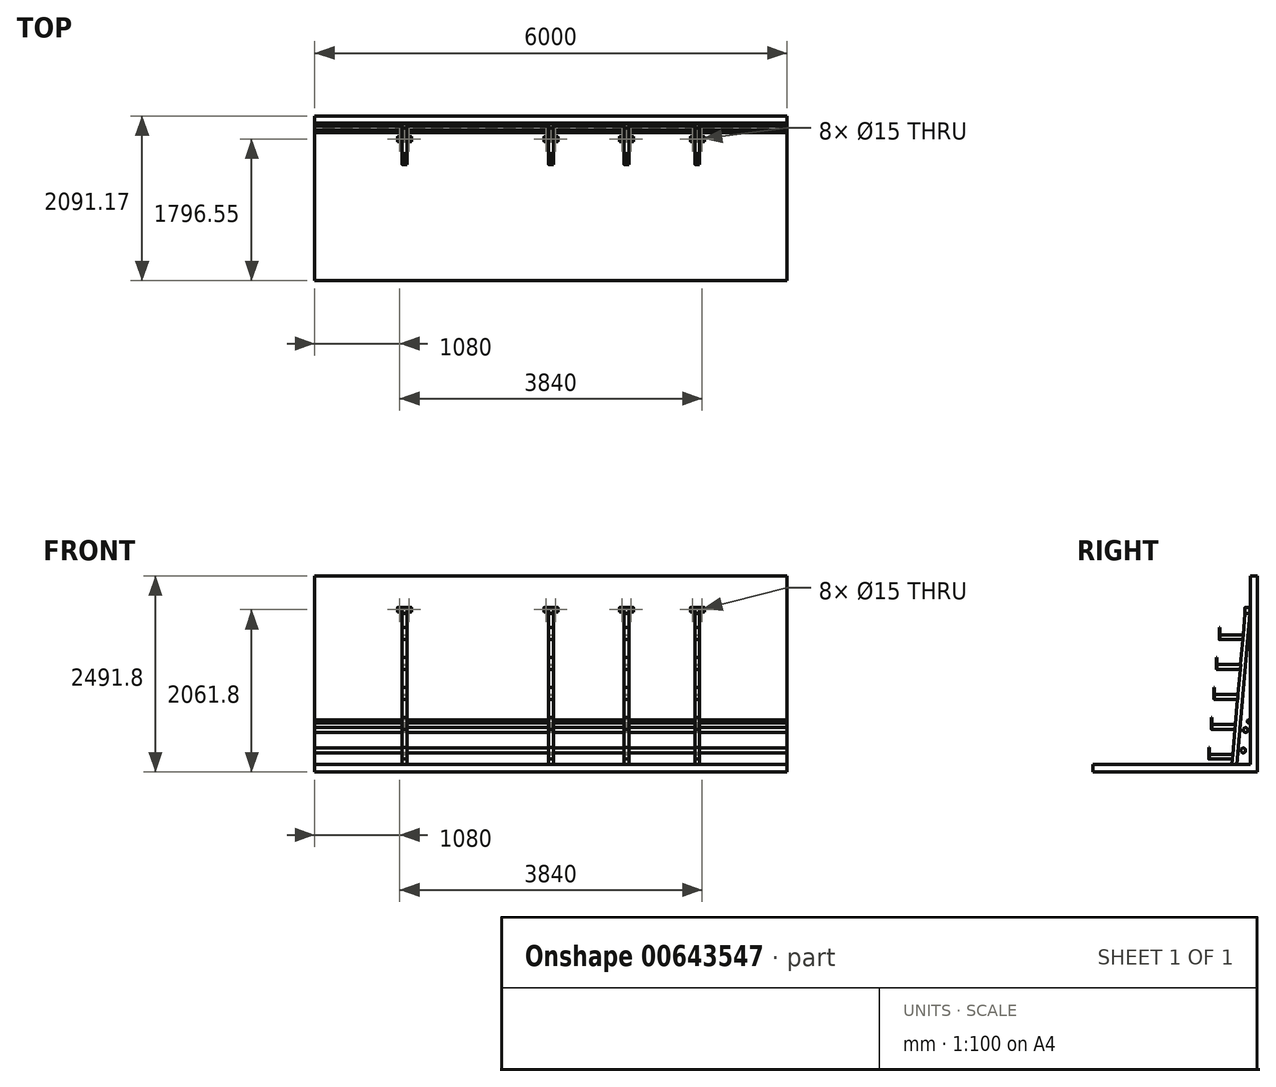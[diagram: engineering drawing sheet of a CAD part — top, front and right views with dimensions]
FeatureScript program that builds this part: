
annotation { "Feature Type Name" : "Feature", "Feature Type Description" : "" }
export const myFeature = defineFeature(function(context is Context, id is Id, definition is map)
    precondition{}
    {
        {
            var Q0;
            Q0=qCreatedBy(makeId("Right.planeOp"),FACE);
            var sketch = newSketch(context, id + "F0", { "sketchPlane" : qUnion([Q0])});
            skLineSegment(sketch, "E0", {"start": v(0, 0) * mm, "end": v(-2000, 0) * mm});
            skLineSegment(sketch, "E1", {"start": v(0, 0) * mm, "end": v(0, 2400) * mm});
            skCircle(sketch, "E2", {"center": v(-60, 440) * mm, "radius": 30 * mm});
            skCircle(sketch, "E3", {"center": v(-20, 550) * mm, "radius": 20 * mm});
            skCircle(sketch, "E4", {"center": v(-90, 180) * mm, "radius": 30 * mm});
            skLineSegment(sketch, "E5.bottom", {"start": v(-2000, 0) * mm, "end": v(0, 0) * mm});
            skLineSegment(sketch, "E5.top", {"start": v(-2000, -91.8) * mm, "end": v(0, -91.8) * mm});
            skLineSegment(sketch, "E5.left", {"start": v(-2000, 0) * mm, "end": v(-2000, -91.8) * mm});
            skLineSegment(sketch, "E6.bottom", {"start": v(0, 2400) * mm, "end": v(91.17, 2400) * mm});
            skLineSegment(sketch, "E6.top", {"start": v(0, -91.8) * mm, "end": v(91.17, -91.8) * mm});
            skLineSegment(sketch, "E6.left", {"start": v(0, 2400) * mm, "end": v(0, 0) * mm});
            skLineSegment(sketch, "E6.right", {"start": v(91.17, 2400) * mm, "end": v(91.17, -91.8) * mm});
            skSolve(sketch);
        }
        {
            var Q0;
            Q0 = qSketchRegion(id + "F0", true);
            extrude(context, id + "F1", {"entities" : qUnion([Q0]), "depth" : 6000 * mm, "offsetDistance" : 25 * mm});
        }
        {
            var Q0;
            Q0=makeQuery(id+"F1.opExtrude","CAP_FACE",FACE,{"disambiguationData":[OSD([sQuery(id+"F0.wireOp",EDGE,"E5.bottom"),sQuery(id+"F0.wireOp",EDGE,"E5.top"),sQuery(id+"F0.wireOp",EDGE,"E5.left"),sQuery(id+"F0.wireOp",EDGE,"E6.bottom"),sQuery(id+"F0.wireOp",EDGE,"E6.top"),sQuery(id+"F0.wireOp",EDGE,"E6.left"),sQuery(id+"F0.wireOp",EDGE,"E6.right")])],"isStart":false});
            var sketch = newSketch(context, id + "F2", { "sketchPlane" : qUnion([Q0])});
            skLineSegment(sketch, "E7", {"start": v(-480, 0) * mm, "end": v(-480, 1226.6) * mm});
            skLineSegment(sketch, "E8", {"start": v(-530, 0) * mm, "end": v(-530, 1239.52) * mm});
            skSolve(sketch);
        }
        {
            var Q0;
            {var subQ1=makeQuery(id+"F1.opExtrude","CAP_EDGE",EDGE,{"disambiguationData":[OSD([sQuery(id+"F0.wireOp",EDGE,"E5.left")])],"isStart":false});Q0=makeQuery(id+"F2.imprint","IMPRINT",FACE,{"disambiguationData":[TD([[makeQuery(id+"F2.imprint","IMPRINT",EDGE,{"derivedFrom":subQ1}),1.0]])]});}
            var sketch = newSketch(context, id + "F3", { "sketchPlane" : qUnion([Q0])});
            skLineSegment(sketch, "E9", {"start": v(-167.45, 6) * mm, "end": v(0, 1920) * mm});
            skLineSegment(sketch, "E10", {"start": v(-227.45, 6) * mm, "end": v(-60, 1920) * mm});
            skLineSegment(sketch, "E11", {"start": v(0, 1920) * mm, "end": v(-60, 1920) * mm});
            skLineSegment(sketch, "E12", {"start": v(-227.45, 6) * mm, "end": v(-167.45, 6) * mm});
            skPoint(sketch, "E13.end.orphan", {"position": v(-167.98, 0) * mm});
            skPoint(sketch, "E13.start.orphan", {"position": v(-227.98, 0) * mm});
            skSolve(sketch);
        }
        {
            var Q0;
            Q0=makeQuery(id+"F3.imprint","IMPRINT",FACE,{"disambiguationData":[TD([[makeQuery(id+"F3.imprint","IMPRINT",EDGE,{"derivedFrom":sQuery(id+"F3.wireOp",EDGE,"E9")}),1.0]])]});
            extrude(context, id + "F4", {"entities" : qUnion([Q0]), "oppositeDirection" : true, "depth" : 60 * mm, "offsetDistance" : 25 * mm});
        }
        {
            var Q0;
            Q0=makeQuery(id+"F4.opExtrude","SWEPT_FACE",FACE,{"disambiguationData":[OSD([sQuery(id+"F3.wireOp",EDGE,"E12")])]});
            var Q1;
            Q1=makeQuery(id+"F4.opExtrude","SWEPT_FACE",FACE,{"disambiguationData":[OSD([sQuery(id+"F3.wireOp",EDGE,"E11")])]});
            shell(context, id + "F5", {"entities" : qUnion([Q0, Q1]), "thickness" : 3 * mm});
        }
        {
            var Q0;
            {var subQ0=sQuery(id+"F3.wireOp",EDGE,"E9");Q0=makeQuery(id+"F5.opShell","OFFSET_EDGE",EDGE,{"disambiguationData":[OSD([subQ0]),TDD([makeQuery(id+"F4.opExtrude","CAP_EDGE",EDGE,{"disambiguationData":[OSD([subQ0])],"isStart":false})])]});}
            var Q1;
            {var subQ0=sQuery(id+"F3.wireOp",EDGE,"E10");Q1=makeQuery(id+"F5.opShell","OFFSET_EDGE",EDGE,{"disambiguationData":[OSD([subQ0]),TDD([makeQuery(id+"F4.opExtrude","CAP_EDGE",EDGE,{"disambiguationData":[OSD([subQ0])],"isStart":false})])]});}
            var Q2;
            {var subQ0=sQuery(id+"F3.wireOp",EDGE,"E9");Q2=makeQuery(id+"F5.opShell","OFFSET_EDGE",EDGE,{"disambiguationData":[OSD([subQ0]),TDD([makeQuery(id+"F4.opExtrude","CAP_EDGE",EDGE,{"disambiguationData":[OSD([subQ0])],"isStart":true})])]});}
            var Q3;
            {var subQ0=sQuery(id+"F3.wireOp",EDGE,"E10");Q3=makeQuery(id+"F5.opShell","OFFSET_EDGE",EDGE,{"disambiguationData":[OSD([subQ0]),TDD([makeQuery(id+"F4.opExtrude","CAP_EDGE",EDGE,{"disambiguationData":[OSD([subQ0])],"isStart":true})])]});}
            fillet(context, id + "F6", {"entities" : qUnion([Q0, Q1, Q2, Q3]), "radius" : 3 * mm, "tangentPropagation" : true, "allowEdgeOverflow" : false});
        }
        {
            var Q0;
            Q0=makeQuery(id+"F4.opExtrude","CAP_EDGE",EDGE,{"disambiguationData":[OSD([sQuery(id+"F3.wireOp",EDGE,"E10")])],"isStart":false});
            var Q1;
            Q1=makeQuery(id+"F4.opExtrude","CAP_EDGE",EDGE,{"disambiguationData":[OSD([sQuery(id+"F3.wireOp",EDGE,"E10")])],"isStart":true});
            var Q2;
            Q2=makeQuery(id+"F4.opExtrude","CAP_EDGE",EDGE,{"disambiguationData":[OSD([sQuery(id+"F3.wireOp",EDGE,"E9")])],"isStart":true});
            var Q3;
            Q3=makeQuery(id+"F4.opExtrude","CAP_EDGE",EDGE,{"disambiguationData":[OSD([sQuery(id+"F3.wireOp",EDGE,"E9")])],"isStart":false});
            fillet(context, id + "F7", {"entities" : qUnion([Q0, Q1, Q2, Q3]), "radius" : 4.5 * mm, "tangentPropagation" : true, "allowEdgeOverflow" : false});
        }
        {
            var Q0;
            Q0=makeQuery(id+"F4.opExtrude","SWEPT_FACE",FACE,{"disambiguationData":[OSD([sQuery(id+"F3.wireOp",EDGE,"E11")])]});
            var sketch = newSketch(context, id + "F8", { "sketchPlane" : qUnion([Q0])});
            skLineSegment(sketch, "E14.0.0", {"start": v(6000, -55.48) * mm, "end": v(6000, -4.52) * mm});
            skEllipticalArc(sketch, "E14.0.1", {});
            skLineSegment(sketch, "E14.0.2", {"start": v(5995.5, 0) * mm, "end": v(5944.5, 0) * mm});
            skEllipticalArc(sketch, "E14.0.3", {});
            skLineSegment(sketch, "E14.0.4", {"start": v(5940, -4.52) * mm, "end": v(5940, -55.48) * mm});
            skEllipticalArc(sketch, "E14.0.5", {});
            skLineSegment(sketch, "E14.0.6", {"start": v(5944.5, -60) * mm, "end": v(5995.5, -60) * mm});
            skEllipticalArc(sketch, "E14.0.7", {});
            skLineSegment(sketch, "E15.0", {"start": v(5946, -56.99) * mm, "end": v(5994, -56.99) * mm});
            skPoint(sketch, "E16.0", {"position": v(5997, -53.98) * mm});
            skEllipticalArc(sketch, "E17.0", {});
            skLineSegment(sketch, "E18.0", {"start": v(5997, -6.02) * mm, "end": v(5997, -53.98) * mm});
            skPoint(sketch, "E19.0", {"position": v(5996.12, -3.9) * mm});
            skEllipticalArc(sketch, "E20.0", {});
            skLineSegment(sketch, "E21.0", {"start": v(5946, -3.01) * mm, "end": v(5994, -3.01) * mm});
            skEllipticalArc(sketch, "E22.0", {});
            skLineSegment(sketch, "E23.0", {"start": v(5943, -6.02) * mm, "end": v(5943, -53.98) * mm});
            skEllipticalArc(sketch, "E24.0", {});
            const initialGuessF8  = {"E14.0.1": [5.9955, -0.0045176047239005035, 0, 1, 0.004517604723900294, 0.0045, 4.71238898038469, 0], "E14.0.3": [5.9445, -0.004517604723900309, 0, -1, 0.004517604723900294, 0.0045, 3.141592653589793, 4.71238898038469], "E14.0.5": [5.9445, -0.05548239527609977, 0, 1, 0.004517604723900294, 0.0045, 1.5707963267948966, 3.141592653589793], "E14.0.7": [5.9955, -0.0554823952760997, 0, -1, 0.004517604723900294, 0.0045, 0, 1.5707963267948966], "E17.0": [5.994, -0.05397652703479969, 0, 1, 0.0030117364826001956, 0.003, 3.141592653589793, 4.71238898038469], "E20.0": [5.994, -0.0060234729652004215, 0, -1, 0.003011736482600195, 0.003, 1.5707963267948966, 3.141592653589793], "E22.0": [5.946, -0.006023472965200574, 0, 1, 0.003011736482600195, 0.003, 0, 1.5707963267948966], "E24.0": [5.946, -0.053976527034799576, 0, -1, 0.0030117364826001956, 0.003, 4.71238898038469, 0]};
            skSetInitialGuess(sketch, initialGuessF8);
            skSolve(sketch);
        }
        {
            var Q0;
            Q0 = qSketchRegion(id + "F8", true);
            extrude(context, id + "F9", {"entities" : qUnion([Q0]), "depth" : 80 * mm, "offsetDistance" : 25 * mm});
        }
        {
            var Q0;
            Q0=makeQuery(id+"F4.opExtrude","CAP_FACE",FACE,{"disambiguationData":[OSD([sQuery(id+"F3.wireOp",EDGE,"E9"),sQuery(id+"F3.wireOp",EDGE,"E10"),sQuery(id+"F3.wireOp",EDGE,"E13"),sQuery(id+"F3.wireOp",EDGE,"E11")])],"isStart":true});
            var sketch = newSketch(context, id + "F10", { "sketchPlane" : qUnion([Q0])});
            skLineSegment(sketch, "E25.0", {"start": v(-228, -0.18) * mm, "end": v(-60, 1920) * mm});
            skLineSegment(sketch, "E26", {"start": v(-221.85, 70) * mm, "end": v(-516.6, 70) * mm});
            skLineSegment(sketch, "E27", {"start": v(-516.6, 70) * mm, "end": v(-516.6, 130) * mm});
            skLineSegment(sketch, "E28", {"start": v(-516.6, 130) * mm, "end": v(-216.6, 130) * mm});
            skLineSegment(sketch, "E29", {"start": v(-216.6, 130) * mm, "end": v(-221.85, 70) * mm});
            skSolve(sketch);
        }
        {
            var Q0;
            Q0 = qSketchRegion(id + "F10", true);
            extrude(context, id + "F11", {"entities" : qUnion([Q0]), "oppositeDirection" : true, "depth" : 60 * mm, "offsetDistance" : 25 * mm});
        }
        {
            var Q0;
            Q0=makeQuery(id+"F11.opExtrude","SWEPT_FACE",FACE,{"disambiguationData":[OSD([sQuery(id+"F10.wireOp",EDGE,"E27")])]});
            var Q1;
            Q1=makeQuery(id+"F11.opExtrude","SWEPT_FACE",FACE,{"disambiguationData":[OSD([sQuery(id+"F10.wireOp",EDGE,"E29")])]});
            shell(context, id + "F12", {"entities" : qUnion([Q0, Q1]), "thickness" : 3 * mm});
        }
        {
            var Q0;
            {var subQ0=sQuery(id+"F10.wireOp",EDGE,"E26");Q0=makeQuery(id+"F12.opShell","OFFSET_EDGE",EDGE,{"disambiguationData":[OSD([subQ0]),TDD([makeQuery(id+"F11.opExtrude","CAP_EDGE",EDGE,{"disambiguationData":[OSD([subQ0])],"isStart":false})])]});}
            var Q1;
            {var subQ0=sQuery(id+"F10.wireOp",EDGE,"E28");Q1=makeQuery(id+"F12.opShell","OFFSET_EDGE",EDGE,{"disambiguationData":[OSD([subQ0]),TDD([makeQuery(id+"F11.opExtrude","CAP_EDGE",EDGE,{"disambiguationData":[OSD([subQ0])],"isStart":false})])]});}
            var Q2;
            {var subQ0=sQuery(id+"F10.wireOp",EDGE,"E28");Q2=makeQuery(id+"F12.opShell","OFFSET_EDGE",EDGE,{"disambiguationData":[OSD([subQ0]),TDD([makeQuery(id+"F11.opExtrude","CAP_EDGE",EDGE,{"disambiguationData":[OSD([subQ0])],"isStart":true})])]});}
            var Q3;
            {var subQ0=sQuery(id+"F10.wireOp",EDGE,"E26");Q3=makeQuery(id+"F12.opShell","OFFSET_EDGE",EDGE,{"disambiguationData":[OSD([subQ0]),TDD([makeQuery(id+"F11.opExtrude","CAP_EDGE",EDGE,{"disambiguationData":[OSD([subQ0])],"isStart":true})])]});}
            fillet(context, id + "F13", {"entities" : qUnion([Q0, Q1, Q2, Q3]), "radius" : 3 * mm, "tangentPropagation" : true, "allowEdgeOverflow" : false});
        }
        {
            var Q0;
            Q0=makeQuery(id+"F11.opExtrude","CAP_EDGE",EDGE,{"disambiguationData":[OSD([sQuery(id+"F10.wireOp",EDGE,"E28")])],"isStart":true});
            var Q1;
            Q1=makeQuery(id+"F11.opExtrude","CAP_EDGE",EDGE,{"disambiguationData":[OSD([sQuery(id+"F10.wireOp",EDGE,"E26")])],"isStart":true});
            var Q2;
            Q2=makeQuery(id+"F11.opExtrude","CAP_EDGE",EDGE,{"disambiguationData":[OSD([sQuery(id+"F10.wireOp",EDGE,"E28")])],"isStart":false});
            var Q3;
            Q3=makeQuery(id+"F11.opExtrude","CAP_EDGE",EDGE,{"disambiguationData":[OSD([sQuery(id+"F10.wireOp",EDGE,"E26")])],"isStart":false});
            fillet(context, id + "F14", {"entities" : qUnion([Q0, Q1, Q2, Q3]), "radius" : 4.5 * mm, "tangentPropagation" : true, "allowEdgeOverflow" : false});
        }
        {
            var Q0;
            Q0=makeQuery(id+"F11.opExtrude","SWEPT_FACE",FACE,{"disambiguationData":[OSD([sQuery(id+"F10.wireOp",EDGE,"E27")])]});
            var sketch = newSketch(context, id + "F15", { "sketchPlane" : qUnion([Q0])});
            skLineSegment(sketch, "E30.bottom", {"start": v(5944.5, 70) * mm, "end": v(5995.5, 70) * mm});
            skLineSegment(sketch, "E30.top", {"start": v(5944.5, 220) * mm, "end": v(5995.5, 220) * mm});
            skLineSegment(sketch, "E30.left", {"start": v(5940, 74.5) * mm, "end": v(5940, 215.5) * mm});
            skLineSegment(sketch, "E30.right", {"start": v(6000, 74.5) * mm, "end": v(6000, 215.5) * mm});
            skPoint(sketch, "E31.visualSharp", {"position": v(5940, 220) * mm});
            skArc(sketch, "E31.filletArc", {"start": v(5944.5, 220) * mm, "mid": v(5941.32, 218.68) * mm, "end": v(5940, 215.5) * mm});
            skPoint(sketch, "E32.visualSharp", {"position": v(6000, 220) * mm});
            skArc(sketch, "E32.filletArc", {"start": v(6000, 215.5) * mm, "mid": v(5998.68, 218.68) * mm, "end": v(5995.5, 220) * mm});
            skPoint(sketch, "E33.visualSharp", {"position": v(6000, 70) * mm});
            skArc(sketch, "E33.filletArc", {"start": v(5995.5, 70) * mm, "mid": v(5998.68, 71.32) * mm, "end": v(6000, 74.5) * mm});
            skPoint(sketch, "E34.visualSharp", {"position": v(5940, 70) * mm});
            skArc(sketch, "E34.filletArc", {"start": v(5940, 74.5) * mm, "mid": v(5941.32, 71.32) * mm, "end": v(5944.5, 70) * mm});
            skSolve(sketch);
        }
        {
            var Q0;
            Q0 = qSketchRegion(id + "F15", true);
            extrude(context, id + "F16", {"entities" : qUnion([Q0]), "depth" : 6 * mm, "offsetDistance" : 25 * mm});
        }
        {
            var Q0;
            Q0=makeQuery(id+"F4.opExtrude","SWEPT_BODY",BODY,{"disambiguationData":[OSD([sQuery(id+"F3.wireOp",EDGE,"E9"),sQuery(id+"F3.wireOp",EDGE,"E10"),sQuery(id+"F3.wireOp",EDGE,"E11"),sQuery(id+"F3.wireOp",EDGE,"E12")])]});
            var Q1;
            Q1=makeQuery(id+"F11.opExtrude","SWEPT_BODY",BODY,{"disambiguationData":[OSD([sQuery(id+"F10.wireOp",EDGE,"E26"),sQuery(id+"F10.wireOp",EDGE,"E27"),sQuery(id+"F10.wireOp",EDGE,"E28"),sQuery(id+"F10.wireOp",EDGE,"E29")])]});
            var Q2;
            Q2=makeQuery(id+"F16.opExtrude","SWEPT_BODY",BODY,{"disambiguationData":[OSD([sQuery(id+"F15.wireOp",EDGE,"E30.bottom"),sQuery(id+"F15.wireOp",EDGE,"E30.top"),sQuery(id+"F15.wireOp",EDGE,"E30.left"),sQuery(id+"F15.wireOp",EDGE,"E30.right"),sQuery(id+"F15.wireOp",EDGE,"E31.filletArc"),sQuery(id+"F15.wireOp",EDGE,"E32.filletArc"),sQuery(id+"F15.wireOp",EDGE,"E33.filletArc"),sQuery(id+"F15.wireOp",EDGE,"E34.filletArc")])]});
            var Q3;
            Q3=makeQuery(id+"F9.opExtrude","SWEPT_BODY",BODY,{"disambiguationData":[OSD([sQuery(id+"F8.wireOp",EDGE,"E14.0.0"),sQuery(id+"F8.wireOp",EDGE,"E14.0.1"),sQuery(id+"F8.wireOp",EDGE,"E14.0.2"),sQuery(id+"F8.wireOp",EDGE,"E14.0.3"),sQuery(id+"F8.wireOp",EDGE,"E14.0.4"),sQuery(id+"F8.wireOp",EDGE,"E14.0.5"),sQuery(id+"F8.wireOp",EDGE,"E14.0.6"),sQuery(id+"F8.wireOp",EDGE,"E14.0.7"),sQuery(id+"F8.wireOp",EDGE,"E15.0"),sQuery(id+"F8.wireOp",EDGE,"E17.0"),sQuery(id+"F8.wireOp",EDGE,"E18.0"),sQuery(id+"F8.wireOp",EDGE,"E20.0"),sQuery(id+"F8.wireOp",EDGE,"E21.0"),sQuery(id+"F8.wireOp",EDGE,"E22.0"),sQuery(id+"F8.wireOp",EDGE,"E23.0"),sQuery(id+"F8.wireOp",EDGE,"E24.0")])]});
            transform(context, id + "F17", {"entities" : qUnion([Q0, Q1, Q2, Q3]), "transformType" : TransformType.TRANSLATION_3D, "dx" : 0 * mm, "dy" : -6 * mm, "dz" : 0 * mm, "makeCopy" : false});
        }
        {
            var Q0;
            Q0=makeQuery(id+"F11.opExtrude","SWEPT_BODY",BODY,{"disambiguationData":[OSD([sQuery(id+"F10.wireOp",EDGE,"E26"),sQuery(id+"F10.wireOp",EDGE,"E27"),sQuery(id+"F10.wireOp",EDGE,"E28"),sQuery(id+"F10.wireOp",EDGE,"E29")])]});
            transform(context, id + "F18", {"entities" : qUnion([Q0]), "transformType" : TransformType.TRANSLATION_3D, "dx" : 0 * mm, "dy" : 33.5 * mm, "dz" : 380 * mm, "makeCopy" : true});
        }
        {
            var Q0;
            Q0=makeQuery(id+"F18.opPattern","COPY",BODY,{"derivedFrom":makeQuery(id+"F11.opExtrude","SWEPT_BODY",BODY,{"disambiguationData":[OSD([sQuery(id+"F10.wireOp",EDGE,"E26"),sQuery(id+"F10.wireOp",EDGE,"E27"),sQuery(id+"F10.wireOp",EDGE,"E28"),sQuery(id+"F10.wireOp",EDGE,"E29")])]}),"instanceName":"1"});
            transform(context, id + "F19", {"entities" : qUnion([Q0]), "transformType" : TransformType.TRANSLATION_3D, "dx" : 0 * mm, "dy" : 33.5 * mm, "dz" : 380 * mm, "makeCopy" : true});
        }
        {
            var Q0;
            Q0=makeQuery(id+"F19.opPattern","COPY",BODY,{"derivedFrom":makeQuery(id+"F18.opPattern","COPY",BODY,{"derivedFrom":makeQuery(id+"F11.opExtrude","SWEPT_BODY",BODY,{"disambiguationData":[OSD([sQuery(id+"F10.wireOp",EDGE,"E26"),sQuery(id+"F10.wireOp",EDGE,"E27"),sQuery(id+"F10.wireOp",EDGE,"E28"),sQuery(id+"F10.wireOp",EDGE,"E29")])]}),"instanceName":"1"}),"instanceName":"1"});
            transform(context, id + "F20", {"entities" : qUnion([Q0]), "transformType" : TransformType.TRANSLATION_3D, "dx" : 0 * mm, "dy" : 33.5 * mm, "dz" : 380 * mm, "makeCopy" : true});
        }
        {
            var Q0;
            Q0=makeQuery(id+"F20.opPattern","COPY",BODY,{"derivedFrom":makeQuery(id+"F19.opPattern","COPY",BODY,{"derivedFrom":makeQuery(id+"F18.opPattern","COPY",BODY,{"derivedFrom":makeQuery(id+"F11.opExtrude","SWEPT_BODY",BODY,{"disambiguationData":[OSD([sQuery(id+"F10.wireOp",EDGE,"E26"),sQuery(id+"F10.wireOp",EDGE,"E27"),sQuery(id+"F10.wireOp",EDGE,"E28"),sQuery(id+"F10.wireOp",EDGE,"E29")])]}),"instanceName":"1"}),"instanceName":"1"}),"instanceName":"1"});
            transform(context, id + "F21", {"entities" : qUnion([Q0]), "transformType" : TransformType.TRANSLATION_3D, "dx" : 0 * mm, "dy" : 33.5 * mm, "dz" : 380 * mm, "makeCopy" : true});
        }
        {
            var Q0;
            Q0=makeQuery(id+"F16.opExtrude","SWEPT_BODY",BODY,{"disambiguationData":[OSD([sQuery(id+"F15.wireOp",EDGE,"E30.bottom"),sQuery(id+"F15.wireOp",EDGE,"E30.top"),sQuery(id+"F15.wireOp",EDGE,"E30.left"),sQuery(id+"F15.wireOp",EDGE,"E30.right"),sQuery(id+"F15.wireOp",EDGE,"E31.filletArc"),sQuery(id+"F15.wireOp",EDGE,"E32.filletArc"),sQuery(id+"F15.wireOp",EDGE,"E33.filletArc"),sQuery(id+"F15.wireOp",EDGE,"E34.filletArc")])]});
            transform(context, id + "F22", {"entities" : qUnion([Q0]), "transformType" : TransformType.TRANSLATION_3D, "dx" : 0 * mm, "dy" : 33.5 * mm, "dz" : 380 * mm, "makeCopy" : true});
        }
        {
            var Q0;
            Q0=makeQuery(id+"F22.opPattern","COPY",BODY,{"derivedFrom":makeQuery(id+"F16.opExtrude","SWEPT_BODY",BODY,{"disambiguationData":[OSD([sQuery(id+"F15.wireOp",EDGE,"E30.bottom"),sQuery(id+"F15.wireOp",EDGE,"E30.top"),sQuery(id+"F15.wireOp",EDGE,"E30.left"),sQuery(id+"F15.wireOp",EDGE,"E30.right"),sQuery(id+"F15.wireOp",EDGE,"E31.filletArc"),sQuery(id+"F15.wireOp",EDGE,"E32.filletArc"),sQuery(id+"F15.wireOp",EDGE,"E33.filletArc"),sQuery(id+"F15.wireOp",EDGE,"E34.filletArc")])]}),"instanceName":"1"});
            transform(context, id + "F23", {"entities" : qUnion([Q0]), "transformType" : TransformType.TRANSLATION_3D, "dx" : 0 * mm, "dy" : 33.5 * mm, "dz" : 380 * mm, "makeCopy" : true});
        }
        {
            var Q0;
            Q0=makeQuery(id+"F23.opPattern","COPY",BODY,{"derivedFrom":makeQuery(id+"F22.opPattern","COPY",BODY,{"derivedFrom":makeQuery(id+"F16.opExtrude","SWEPT_BODY",BODY,{"disambiguationData":[OSD([sQuery(id+"F15.wireOp",EDGE,"E30.bottom"),sQuery(id+"F15.wireOp",EDGE,"E30.top"),sQuery(id+"F15.wireOp",EDGE,"E30.left"),sQuery(id+"F15.wireOp",EDGE,"E30.right"),sQuery(id+"F15.wireOp",EDGE,"E31.filletArc"),sQuery(id+"F15.wireOp",EDGE,"E32.filletArc"),sQuery(id+"F15.wireOp",EDGE,"E33.filletArc"),sQuery(id+"F15.wireOp",EDGE,"E34.filletArc")])]}),"instanceName":"1"}),"instanceName":"1"});
            transform(context, id + "F24", {"entities" : qUnion([Q0]), "transformType" : TransformType.TRANSLATION_3D, "dx" : 0 * mm, "dy" : 33.5 * mm, "dz" : 380 * mm, "makeCopy" : true});
        }
        {
            var Q0;
            Q0=makeQuery(id+"F24.opPattern","COPY",BODY,{"derivedFrom":makeQuery(id+"F23.opPattern","COPY",BODY,{"derivedFrom":makeQuery(id+"F22.opPattern","COPY",BODY,{"derivedFrom":makeQuery(id+"F16.opExtrude","SWEPT_BODY",BODY,{"disambiguationData":[OSD([sQuery(id+"F15.wireOp",EDGE,"E30.bottom"),sQuery(id+"F15.wireOp",EDGE,"E30.top"),sQuery(id+"F15.wireOp",EDGE,"E30.left"),sQuery(id+"F15.wireOp",EDGE,"E30.right"),sQuery(id+"F15.wireOp",EDGE,"E31.filletArc"),sQuery(id+"F15.wireOp",EDGE,"E32.filletArc"),sQuery(id+"F15.wireOp",EDGE,"E33.filletArc"),sQuery(id+"F15.wireOp",EDGE,"E34.filletArc")])]}),"instanceName":"1"}),"instanceName":"1"}),"instanceName":"1"});
            transform(context, id + "F25", {"entities" : qUnion([Q0]), "transformType" : TransformType.TRANSLATION_3D, "dx" : 0 * mm, "dy" : 33.5 * mm, "dz" : 380 * mm, "makeCopy" : true});
        }
        {
            var Q0;
            Q0=makeQuery(id+"F4.opExtrude","SWEPT_FACE",FACE,{"disambiguationData":[OSD([sQuery(id+"F3.wireOp",EDGE,"E12")])]});
            var sketch = newSketch(context, id + "F26", { "sketchPlane" : qUnion([Q0])});
            skLineSegment(sketch, "E35.bottom", {"start": v(6055.5, 173.45) * mm, "end": v(5884.5, 173.45) * mm});
            skLineSegment(sketch, "E35.top", {"start": v(6055.5, 233.45) * mm, "end": v(5884.5, 233.45) * mm});
            skLineSegment(sketch, "E35.left", {"start": v(6060, 177.95) * mm, "end": v(6060, 228.95) * mm});
            skLineSegment(sketch, "E35.right", {"start": v(5880, 177.95) * mm, "end": v(5880, 228.95) * mm});
            skPoint(sketch, "E36.visualSharp", {"position": v(6060, 173.45) * mm});
            skArc(sketch, "E36.filletArc", {"start": v(6055.5, 173.45) * mm, "mid": v(6058.68, 174.77) * mm, "end": v(6060, 177.95) * mm});
            skPoint(sketch, "E37.visualSharp", {"position": v(6060, 233.45) * mm});
            skArc(sketch, "E37.filletArc", {"start": v(6060, 228.95) * mm, "mid": v(6058.68, 232.14) * mm, "end": v(6055.5, 233.45) * mm});
            skPoint(sketch, "E38.visualSharp", {"position": v(5880, 233.45) * mm});
            skArc(sketch, "E38.filletArc", {"start": v(5884.5, 233.45) * mm, "mid": v(5881.32, 232.14) * mm, "end": v(5880, 228.95) * mm});
            skPoint(sketch, "E39.visualSharp", {"position": v(5880, 173.45) * mm});
            skArc(sketch, "E39.filletArc", {"start": v(5880, 177.95) * mm, "mid": v(5881.32, 174.77) * mm, "end": v(5884.5, 173.45) * mm});
            skCircle(sketch, "E40", {"center": v(6030, 203.45) * mm, "radius": 7.5 * mm});
            skCircle(sketch, "E41", {"center": v(5910, 203.45) * mm, "radius": 7.5 * mm});
            skSolve(sketch);
        }
        {
            var Q0;
            Q0 = qSketchRegion(id + "F26", true);
            extrude(context, id + "F27", {"entities" : qUnion([Q0]), "depth" : 6 * mm, "offsetDistance" : 25 * mm});
        }
        {
            var Q0;
            Q0=makeQuery(id+"F9.opExtrude","SWEPT_FACE",FACE,{"disambiguationData":[OSD([sQuery(id+"F8.wireOp",EDGE,"E14.0.2")])]});
            var sketch = newSketch(context, id + "F28", { "sketchPlane" : qUnion([Q0])});
            skLineSegment(sketch, "E42.bottom", {"start": v(-5884.5, 1940) * mm, "end": v(-6055.5, 1940) * mm});
            skLineSegment(sketch, "E42.top", {"start": v(-5884.5, 2000) * mm, "end": v(-6055.5, 2000) * mm});
            skLineSegment(sketch, "E42.left", {"start": v(-5880, 1944.5) * mm, "end": v(-5880, 1995.5) * mm});
            skLineSegment(sketch, "E42.right", {"start": v(-6060, 1944.5) * mm, "end": v(-6060, 1995.5) * mm});
            skCircle(sketch, "E43", {"center": v(-5910, 1970) * mm, "radius": 7.5 * mm});
            skCircle(sketch, "E44", {"center": v(-6030, 1970) * mm, "radius": 7.5 * mm});
            skPoint(sketch, "E45.visualSharp", {"position": v(-5880, 1940) * mm});
            skArc(sketch, "E45.filletArc", {"start": v(-5884.5, 1940) * mm, "mid": v(-5881.32, 1941.32) * mm, "end": v(-5880, 1944.5) * mm});
            skPoint(sketch, "E46.visualSharp", {"position": v(-5880, 2000) * mm});
            skArc(sketch, "E46.filletArc", {"start": v(-5880, 1995.5) * mm, "mid": v(-5881.32, 1998.68) * mm, "end": v(-5884.5, 2000) * mm});
            skPoint(sketch, "E47.visualSharp", {"position": v(-6060, 2000) * mm});
            skArc(sketch, "E47.filletArc", {"start": v(-6055.5, 2000) * mm, "mid": v(-6058.68, 1998.68) * mm, "end": v(-6060, 1995.5) * mm});
            skPoint(sketch, "E48.visualSharp", {"position": v(-6060, 1940) * mm});
            skArc(sketch, "E48.filletArc", {"start": v(-6060, 1944.5) * mm, "mid": v(-6058.68, 1941.32) * mm, "end": v(-6055.5, 1940) * mm});
            skSolve(sketch);
        }
        {
            var Q0;
            Q0 = qSketchRegion(id + "F28", true);
            extrude(context, id + "F29", {"entities" : qUnion([Q0]), "depth" : 6 * mm, "offsetDistance" : 25 * mm});
        }
        {
            var Q0;
            Q0=makeQuery(id+"F4.opExtrude","SWEPT_BODY",BODY,{"disambiguationData":[OSD([sQuery(id+"F3.wireOp",EDGE,"E9"),sQuery(id+"F3.wireOp",EDGE,"E10"),sQuery(id+"F3.wireOp",EDGE,"E11"),sQuery(id+"F3.wireOp",EDGE,"E12")])]});
            var Q1;
            Q1=makeQuery(id+"F9.opExtrude","SWEPT_BODY",BODY,{"disambiguationData":[OSD([sQuery(id+"F8.wireOp",EDGE,"E14.0.0"),sQuery(id+"F8.wireOp",EDGE,"E14.0.1"),sQuery(id+"F8.wireOp",EDGE,"E14.0.2"),sQuery(id+"F8.wireOp",EDGE,"E14.0.3"),sQuery(id+"F8.wireOp",EDGE,"E14.0.4"),sQuery(id+"F8.wireOp",EDGE,"E14.0.5"),sQuery(id+"F8.wireOp",EDGE,"E14.0.6"),sQuery(id+"F8.wireOp",EDGE,"E14.0.7"),sQuery(id+"F8.wireOp",EDGE,"E15.0"),sQuery(id+"F8.wireOp",EDGE,"E17.0"),sQuery(id+"F8.wireOp",EDGE,"E18.0"),sQuery(id+"F8.wireOp",EDGE,"E20.0"),sQuery(id+"F8.wireOp",EDGE,"E21.0"),sQuery(id+"F8.wireOp",EDGE,"E22.0"),sQuery(id+"F8.wireOp",EDGE,"E23.0"),sQuery(id+"F8.wireOp",EDGE,"E24.0")])]});
            var Q2;
            Q2=makeQuery(id+"F21.opPattern","COPY",BODY,{"derivedFrom":makeQuery(id+"F20.opPattern","COPY",BODY,{"derivedFrom":makeQuery(id+"F19.opPattern","COPY",BODY,{"derivedFrom":makeQuery(id+"F18.opPattern","COPY",BODY,{"derivedFrom":makeQuery(id+"F11.opExtrude","SWEPT_BODY",BODY,{"disambiguationData":[OSD([sQuery(id+"F10.wireOp",EDGE,"E26"),sQuery(id+"F10.wireOp",EDGE,"E27"),sQuery(id+"F10.wireOp",EDGE,"E28"),sQuery(id+"F10.wireOp",EDGE,"E29")])]}),"instanceName":"1"}),"instanceName":"1"}),"instanceName":"1"}),"instanceName":"1"});
            var Q3;
            Q3=makeQuery(id+"F25.opPattern","COPY",BODY,{"derivedFrom":makeQuery(id+"F24.opPattern","COPY",BODY,{"derivedFrom":makeQuery(id+"F23.opPattern","COPY",BODY,{"derivedFrom":makeQuery(id+"F22.opPattern","COPY",BODY,{"derivedFrom":makeQuery(id+"F16.opExtrude","SWEPT_BODY",BODY,{"disambiguationData":[OSD([sQuery(id+"F15.wireOp",EDGE,"E30.bottom"),sQuery(id+"F15.wireOp",EDGE,"E30.top"),sQuery(id+"F15.wireOp",EDGE,"E30.left"),sQuery(id+"F15.wireOp",EDGE,"E30.right"),sQuery(id+"F15.wireOp",EDGE,"E31.filletArc"),sQuery(id+"F15.wireOp",EDGE,"E32.filletArc"),sQuery(id+"F15.wireOp",EDGE,"E33.filletArc"),sQuery(id+"F15.wireOp",EDGE,"E34.filletArc")])]}),"instanceName":"1"}),"instanceName":"1"}),"instanceName":"1"}),"instanceName":"1"});
            var Q4;
            Q4=makeQuery(id+"F24.opPattern","COPY",BODY,{"derivedFrom":makeQuery(id+"F23.opPattern","COPY",BODY,{"derivedFrom":makeQuery(id+"F22.opPattern","COPY",BODY,{"derivedFrom":makeQuery(id+"F16.opExtrude","SWEPT_BODY",BODY,{"disambiguationData":[OSD([sQuery(id+"F15.wireOp",EDGE,"E30.bottom"),sQuery(id+"F15.wireOp",EDGE,"E30.top"),sQuery(id+"F15.wireOp",EDGE,"E30.left"),sQuery(id+"F15.wireOp",EDGE,"E30.right"),sQuery(id+"F15.wireOp",EDGE,"E31.filletArc"),sQuery(id+"F15.wireOp",EDGE,"E32.filletArc"),sQuery(id+"F15.wireOp",EDGE,"E33.filletArc"),sQuery(id+"F15.wireOp",EDGE,"E34.filletArc")])]}),"instanceName":"1"}),"instanceName":"1"}),"instanceName":"1"});
            var Q5;
            Q5=makeQuery(id+"F20.opPattern","COPY",BODY,{"derivedFrom":makeQuery(id+"F19.opPattern","COPY",BODY,{"derivedFrom":makeQuery(id+"F18.opPattern","COPY",BODY,{"derivedFrom":makeQuery(id+"F11.opExtrude","SWEPT_BODY",BODY,{"disambiguationData":[OSD([sQuery(id+"F10.wireOp",EDGE,"E26"),sQuery(id+"F10.wireOp",EDGE,"E27"),sQuery(id+"F10.wireOp",EDGE,"E28"),sQuery(id+"F10.wireOp",EDGE,"E29")])]}),"instanceName":"1"}),"instanceName":"1"}),"instanceName":"1"});
            var Q6;
            Q6=makeQuery(id+"F19.opPattern","COPY",BODY,{"derivedFrom":makeQuery(id+"F18.opPattern","COPY",BODY,{"derivedFrom":makeQuery(id+"F11.opExtrude","SWEPT_BODY",BODY,{"disambiguationData":[OSD([sQuery(id+"F10.wireOp",EDGE,"E26"),sQuery(id+"F10.wireOp",EDGE,"E27"),sQuery(id+"F10.wireOp",EDGE,"E28"),sQuery(id+"F10.wireOp",EDGE,"E29")])]}),"instanceName":"1"}),"instanceName":"1"});
            var Q7;
            Q7=makeQuery(id+"F23.opPattern","COPY",BODY,{"derivedFrom":makeQuery(id+"F22.opPattern","COPY",BODY,{"derivedFrom":makeQuery(id+"F16.opExtrude","SWEPT_BODY",BODY,{"disambiguationData":[OSD([sQuery(id+"F15.wireOp",EDGE,"E30.bottom"),sQuery(id+"F15.wireOp",EDGE,"E30.top"),sQuery(id+"F15.wireOp",EDGE,"E30.left"),sQuery(id+"F15.wireOp",EDGE,"E30.right"),sQuery(id+"F15.wireOp",EDGE,"E31.filletArc"),sQuery(id+"F15.wireOp",EDGE,"E32.filletArc"),sQuery(id+"F15.wireOp",EDGE,"E33.filletArc"),sQuery(id+"F15.wireOp",EDGE,"E34.filletArc")])]}),"instanceName":"1"}),"instanceName":"1"});
            var Q8;
            Q8=makeQuery(id+"F22.opPattern","COPY",BODY,{"derivedFrom":makeQuery(id+"F16.opExtrude","SWEPT_BODY",BODY,{"disambiguationData":[OSD([sQuery(id+"F15.wireOp",EDGE,"E30.bottom"),sQuery(id+"F15.wireOp",EDGE,"E30.top"),sQuery(id+"F15.wireOp",EDGE,"E30.left"),sQuery(id+"F15.wireOp",EDGE,"E30.right"),sQuery(id+"F15.wireOp",EDGE,"E31.filletArc"),sQuery(id+"F15.wireOp",EDGE,"E32.filletArc"),sQuery(id+"F15.wireOp",EDGE,"E33.filletArc"),sQuery(id+"F15.wireOp",EDGE,"E34.filletArc")])]}),"instanceName":"1"});
            var Q9;
            Q9=makeQuery(id+"F18.opPattern","COPY",BODY,{"derivedFrom":makeQuery(id+"F11.opExtrude","SWEPT_BODY",BODY,{"disambiguationData":[OSD([sQuery(id+"F10.wireOp",EDGE,"E26"),sQuery(id+"F10.wireOp",EDGE,"E27"),sQuery(id+"F10.wireOp",EDGE,"E28"),sQuery(id+"F10.wireOp",EDGE,"E29")])]}),"instanceName":"1"});
            var Q10;
            Q10=makeQuery(id+"F11.opExtrude","SWEPT_BODY",BODY,{"disambiguationData":[OSD([sQuery(id+"F10.wireOp",EDGE,"E26"),sQuery(id+"F10.wireOp",EDGE,"E27"),sQuery(id+"F10.wireOp",EDGE,"E28"),sQuery(id+"F10.wireOp",EDGE,"E29")])]});
            var Q11;
            Q11=makeQuery(id+"F16.opExtrude","SWEPT_BODY",BODY,{"disambiguationData":[OSD([sQuery(id+"F15.wireOp",EDGE,"E30.bottom"),sQuery(id+"F15.wireOp",EDGE,"E30.top"),sQuery(id+"F15.wireOp",EDGE,"E30.left"),sQuery(id+"F15.wireOp",EDGE,"E30.right"),sQuery(id+"F15.wireOp",EDGE,"E31.filletArc"),sQuery(id+"F15.wireOp",EDGE,"E32.filletArc"),sQuery(id+"F15.wireOp",EDGE,"E33.filletArc"),sQuery(id+"F15.wireOp",EDGE,"E34.filletArc")])]});
            var Q12;
            Q12=makeQuery(id+"F27.opExtrude","SWEPT_BODY",BODY,{"disambiguationData":[OSD([sQuery(id+"F26.wireOp",EDGE,"E35.bottom"),sQuery(id+"F26.wireOp",EDGE,"E35.top"),sQuery(id+"F26.wireOp",EDGE,"E35.left"),sQuery(id+"F26.wireOp",EDGE,"E35.right"),sQuery(id+"F26.wireOp",EDGE,"E36.filletArc"),sQuery(id+"F26.wireOp",EDGE,"E37.filletArc"),sQuery(id+"F26.wireOp",EDGE,"E38.filletArc"),sQuery(id+"F26.wireOp",EDGE,"E39.filletArc"),sQuery(id+"F26.wireOp",EDGE,"E40"),sQuery(id+"F26.wireOp",EDGE,"E41")])]});
            var Q13;
            Q13=makeQuery(id+"F29.opExtrude","SWEPT_BODY",BODY,{"disambiguationData":[OSD([sQuery(id+"F28.wireOp",EDGE,"E42.bottom"),sQuery(id+"F28.wireOp",EDGE,"E42.top"),sQuery(id+"F28.wireOp",EDGE,"E42.left"),sQuery(id+"F28.wireOp",EDGE,"E42.right"),sQuery(id+"F28.wireOp",EDGE,"E43"),sQuery(id+"F28.wireOp",EDGE,"E44"),sQuery(id+"F28.wireOp",EDGE,"E45.filletArc"),sQuery(id+"F28.wireOp",EDGE,"E46.filletArc"),sQuery(id+"F28.wireOp",EDGE,"E47.filletArc"),sQuery(id+"F28.wireOp",EDGE,"E48.filletArc")])]});
            transform(context, id + "F30", {"entities" : qUnion([Q0, Q1, Q2, Q3, Q4, Q5, Q6, Q7, Q8, Q9, Q10, Q11, Q12, Q13]), "transformType" : TransformType.TRANSLATION_3D, "dx" : -2970 * mm, "dy" : 0 * mm, "dz" : 0 * mm, "makeCopy" : false});
        }
        {
            var Q0;
            Q0=makeQuery(id+"F9.opExtrude","SWEPT_BODY",BODY,{"disambiguationData":[OSD([sQuery(id+"F8.wireOp",EDGE,"E14.0.0"),sQuery(id+"F8.wireOp",EDGE,"E14.0.1"),sQuery(id+"F8.wireOp",EDGE,"E14.0.2"),sQuery(id+"F8.wireOp",EDGE,"E14.0.3"),sQuery(id+"F8.wireOp",EDGE,"E14.0.4"),sQuery(id+"F8.wireOp",EDGE,"E14.0.5"),sQuery(id+"F8.wireOp",EDGE,"E14.0.6"),sQuery(id+"F8.wireOp",EDGE,"E14.0.7"),sQuery(id+"F8.wireOp",EDGE,"E15.0"),sQuery(id+"F8.wireOp",EDGE,"E17.0"),sQuery(id+"F8.wireOp",EDGE,"E18.0"),sQuery(id+"F8.wireOp",EDGE,"E20.0"),sQuery(id+"F8.wireOp",EDGE,"E21.0"),sQuery(id+"F8.wireOp",EDGE,"E22.0"),sQuery(id+"F8.wireOp",EDGE,"E23.0"),sQuery(id+"F8.wireOp",EDGE,"E24.0")])]});
            var Q1;
            Q1=makeQuery(id+"F4.opExtrude","SWEPT_BODY",BODY,{"disambiguationData":[OSD([sQuery(id+"F3.wireOp",EDGE,"E9"),sQuery(id+"F3.wireOp",EDGE,"E10"),sQuery(id+"F3.wireOp",EDGE,"E11"),sQuery(id+"F3.wireOp",EDGE,"E12")])]});
            var Q2;
            Q2=makeQuery(id+"F21.opPattern","COPY",BODY,{"derivedFrom":makeQuery(id+"F20.opPattern","COPY",BODY,{"derivedFrom":makeQuery(id+"F19.opPattern","COPY",BODY,{"derivedFrom":makeQuery(id+"F18.opPattern","COPY",BODY,{"derivedFrom":makeQuery(id+"F11.opExtrude","SWEPT_BODY",BODY,{"disambiguationData":[OSD([sQuery(id+"F10.wireOp",EDGE,"E26"),sQuery(id+"F10.wireOp",EDGE,"E27"),sQuery(id+"F10.wireOp",EDGE,"E28"),sQuery(id+"F10.wireOp",EDGE,"E29")])]}),"instanceName":"1"}),"instanceName":"1"}),"instanceName":"1"}),"instanceName":"1"});
            var Q3;
            Q3=makeQuery(id+"F25.opPattern","COPY",BODY,{"derivedFrom":makeQuery(id+"F24.opPattern","COPY",BODY,{"derivedFrom":makeQuery(id+"F23.opPattern","COPY",BODY,{"derivedFrom":makeQuery(id+"F22.opPattern","COPY",BODY,{"derivedFrom":makeQuery(id+"F16.opExtrude","SWEPT_BODY",BODY,{"disambiguationData":[OSD([sQuery(id+"F15.wireOp",EDGE,"E30.bottom"),sQuery(id+"F15.wireOp",EDGE,"E30.top"),sQuery(id+"F15.wireOp",EDGE,"E30.left"),sQuery(id+"F15.wireOp",EDGE,"E30.right"),sQuery(id+"F15.wireOp",EDGE,"E31.filletArc"),sQuery(id+"F15.wireOp",EDGE,"E32.filletArc"),sQuery(id+"F15.wireOp",EDGE,"E33.filletArc"),sQuery(id+"F15.wireOp",EDGE,"E34.filletArc")])]}),"instanceName":"1"}),"instanceName":"1"}),"instanceName":"1"}),"instanceName":"1"});
            var Q4;
            Q4=makeQuery(id+"F24.opPattern","COPY",BODY,{"derivedFrom":makeQuery(id+"F23.opPattern","COPY",BODY,{"derivedFrom":makeQuery(id+"F22.opPattern","COPY",BODY,{"derivedFrom":makeQuery(id+"F16.opExtrude","SWEPT_BODY",BODY,{"disambiguationData":[OSD([sQuery(id+"F15.wireOp",EDGE,"E30.bottom"),sQuery(id+"F15.wireOp",EDGE,"E30.top"),sQuery(id+"F15.wireOp",EDGE,"E30.left"),sQuery(id+"F15.wireOp",EDGE,"E30.right"),sQuery(id+"F15.wireOp",EDGE,"E31.filletArc"),sQuery(id+"F15.wireOp",EDGE,"E32.filletArc"),sQuery(id+"F15.wireOp",EDGE,"E33.filletArc"),sQuery(id+"F15.wireOp",EDGE,"E34.filletArc")])]}),"instanceName":"1"}),"instanceName":"1"}),"instanceName":"1"});
            var Q5;
            Q5=makeQuery(id+"F20.opPattern","COPY",BODY,{"derivedFrom":makeQuery(id+"F19.opPattern","COPY",BODY,{"derivedFrom":makeQuery(id+"F18.opPattern","COPY",BODY,{"derivedFrom":makeQuery(id+"F11.opExtrude","SWEPT_BODY",BODY,{"disambiguationData":[OSD([sQuery(id+"F10.wireOp",EDGE,"E26"),sQuery(id+"F10.wireOp",EDGE,"E27"),sQuery(id+"F10.wireOp",EDGE,"E28"),sQuery(id+"F10.wireOp",EDGE,"E29")])]}),"instanceName":"1"}),"instanceName":"1"}),"instanceName":"1"});
            var Q6;
            Q6=makeQuery(id+"F23.opPattern","COPY",BODY,{"derivedFrom":makeQuery(id+"F22.opPattern","COPY",BODY,{"derivedFrom":makeQuery(id+"F16.opExtrude","SWEPT_BODY",BODY,{"disambiguationData":[OSD([sQuery(id+"F15.wireOp",EDGE,"E30.bottom"),sQuery(id+"F15.wireOp",EDGE,"E30.top"),sQuery(id+"F15.wireOp",EDGE,"E30.left"),sQuery(id+"F15.wireOp",EDGE,"E30.right"),sQuery(id+"F15.wireOp",EDGE,"E31.filletArc"),sQuery(id+"F15.wireOp",EDGE,"E32.filletArc"),sQuery(id+"F15.wireOp",EDGE,"E33.filletArc"),sQuery(id+"F15.wireOp",EDGE,"E34.filletArc")])]}),"instanceName":"1"}),"instanceName":"1"});
            var Q7;
            Q7=makeQuery(id+"F19.opPattern","COPY",BODY,{"derivedFrom":makeQuery(id+"F18.opPattern","COPY",BODY,{"derivedFrom":makeQuery(id+"F11.opExtrude","SWEPT_BODY",BODY,{"disambiguationData":[OSD([sQuery(id+"F10.wireOp",EDGE,"E26"),sQuery(id+"F10.wireOp",EDGE,"E27"),sQuery(id+"F10.wireOp",EDGE,"E28"),sQuery(id+"F10.wireOp",EDGE,"E29")])]}),"instanceName":"1"}),"instanceName":"1"});
            var Q8;
            Q8=makeQuery(id+"F22.opPattern","COPY",BODY,{"derivedFrom":makeQuery(id+"F16.opExtrude","SWEPT_BODY",BODY,{"disambiguationData":[OSD([sQuery(id+"F15.wireOp",EDGE,"E30.bottom"),sQuery(id+"F15.wireOp",EDGE,"E30.top"),sQuery(id+"F15.wireOp",EDGE,"E30.left"),sQuery(id+"F15.wireOp",EDGE,"E30.right"),sQuery(id+"F15.wireOp",EDGE,"E31.filletArc"),sQuery(id+"F15.wireOp",EDGE,"E32.filletArc"),sQuery(id+"F15.wireOp",EDGE,"E33.filletArc"),sQuery(id+"F15.wireOp",EDGE,"E34.filletArc")])]}),"instanceName":"1"});
            var Q9;
            Q9=makeQuery(id+"F18.opPattern","COPY",BODY,{"derivedFrom":makeQuery(id+"F11.opExtrude","SWEPT_BODY",BODY,{"disambiguationData":[OSD([sQuery(id+"F10.wireOp",EDGE,"E26"),sQuery(id+"F10.wireOp",EDGE,"E27"),sQuery(id+"F10.wireOp",EDGE,"E28"),sQuery(id+"F10.wireOp",EDGE,"E29")])]}),"instanceName":"1"});
            var Q10;
            Q10=makeQuery(id+"F16.opExtrude","SWEPT_BODY",BODY,{"disambiguationData":[OSD([sQuery(id+"F15.wireOp",EDGE,"E30.bottom"),sQuery(id+"F15.wireOp",EDGE,"E30.top"),sQuery(id+"F15.wireOp",EDGE,"E30.left"),sQuery(id+"F15.wireOp",EDGE,"E30.right"),sQuery(id+"F15.wireOp",EDGE,"E31.filletArc"),sQuery(id+"F15.wireOp",EDGE,"E32.filletArc"),sQuery(id+"F15.wireOp",EDGE,"E33.filletArc"),sQuery(id+"F15.wireOp",EDGE,"E34.filletArc")])]});
            var Q11;
            Q11=makeQuery(id+"F11.opExtrude","SWEPT_BODY",BODY,{"disambiguationData":[OSD([sQuery(id+"F10.wireOp",EDGE,"E26"),sQuery(id+"F10.wireOp",EDGE,"E27"),sQuery(id+"F10.wireOp",EDGE,"E28"),sQuery(id+"F10.wireOp",EDGE,"E29")])]});
            var Q12;
            Q12=makeQuery(id+"F27.opExtrude","SWEPT_BODY",BODY,{"disambiguationData":[OSD([sQuery(id+"F26.wireOp",EDGE,"E35.bottom"),sQuery(id+"F26.wireOp",EDGE,"E35.top"),sQuery(id+"F26.wireOp",EDGE,"E35.left"),sQuery(id+"F26.wireOp",EDGE,"E35.right"),sQuery(id+"F26.wireOp",EDGE,"E36.filletArc"),sQuery(id+"F26.wireOp",EDGE,"E37.filletArc"),sQuery(id+"F26.wireOp",EDGE,"E38.filletArc"),sQuery(id+"F26.wireOp",EDGE,"E39.filletArc"),sQuery(id+"F26.wireOp",EDGE,"E40"),sQuery(id+"F26.wireOp",EDGE,"E41")])]});
            var Q13;
            Q13=makeQuery(id+"F29.opExtrude","SWEPT_BODY",BODY,{"disambiguationData":[OSD([sQuery(id+"F28.wireOp",EDGE,"E42.bottom"),sQuery(id+"F28.wireOp",EDGE,"E42.top"),sQuery(id+"F28.wireOp",EDGE,"E42.left"),sQuery(id+"F28.wireOp",EDGE,"E42.right"),sQuery(id+"F28.wireOp",EDGE,"E43"),sQuery(id+"F28.wireOp",EDGE,"E44"),sQuery(id+"F28.wireOp",EDGE,"E45.filletArc"),sQuery(id+"F28.wireOp",EDGE,"E46.filletArc"),sQuery(id+"F28.wireOp",EDGE,"E47.filletArc"),sQuery(id+"F28.wireOp",EDGE,"E48.filletArc")])]});
            transform(context, id + "F31", {"entities" : qUnion([Q0, Q1, Q2, Q3, Q4, Q5, Q6, Q7, Q8, Q9, Q10, Q11, Q12, Q13]), "transformType" : TransformType.TRANSLATION_3D, "dx" : 1860 * mm, "dy" : 0 * mm, "dz" : 0 * mm, "makeCopy" : true});
        }
        {
            var Q0;
            Q0=makeQuery(id+"F19.opPattern","COPY",BODY,{"derivedFrom":makeQuery(id+"F18.opPattern","COPY",BODY,{"derivedFrom":makeQuery(id+"F11.opExtrude","SWEPT_BODY",BODY,{"disambiguationData":[OSD([sQuery(id+"F10.wireOp",EDGE,"E26"),sQuery(id+"F10.wireOp",EDGE,"E27"),sQuery(id+"F10.wireOp",EDGE,"E28"),sQuery(id+"F10.wireOp",EDGE,"E29")])]}),"instanceName":"1"}),"instanceName":"1"});
            var Q1;
            Q1=makeQuery(id+"F9.opExtrude","SWEPT_BODY",BODY,{"disambiguationData":[OSD([sQuery(id+"F8.wireOp",EDGE,"E14.0.0"),sQuery(id+"F8.wireOp",EDGE,"E14.0.1"),sQuery(id+"F8.wireOp",EDGE,"E14.0.2"),sQuery(id+"F8.wireOp",EDGE,"E14.0.3"),sQuery(id+"F8.wireOp",EDGE,"E14.0.4"),sQuery(id+"F8.wireOp",EDGE,"E14.0.5"),sQuery(id+"F8.wireOp",EDGE,"E14.0.6"),sQuery(id+"F8.wireOp",EDGE,"E14.0.7"),sQuery(id+"F8.wireOp",EDGE,"E15.0"),sQuery(id+"F8.wireOp",EDGE,"E17.0"),sQuery(id+"F8.wireOp",EDGE,"E18.0"),sQuery(id+"F8.wireOp",EDGE,"E20.0"),sQuery(id+"F8.wireOp",EDGE,"E21.0"),sQuery(id+"F8.wireOp",EDGE,"E22.0"),sQuery(id+"F8.wireOp",EDGE,"E23.0"),sQuery(id+"F8.wireOp",EDGE,"E24.0")])]});
            var Q2;
            Q2=makeQuery(id+"F4.opExtrude","SWEPT_BODY",BODY,{"disambiguationData":[OSD([sQuery(id+"F3.wireOp",EDGE,"E9"),sQuery(id+"F3.wireOp",EDGE,"E10"),sQuery(id+"F3.wireOp",EDGE,"E11"),sQuery(id+"F3.wireOp",EDGE,"E12")])]});
            var Q3;
            Q3=makeQuery(id+"F21.opPattern","COPY",BODY,{"derivedFrom":makeQuery(id+"F20.opPattern","COPY",BODY,{"derivedFrom":makeQuery(id+"F19.opPattern","COPY",BODY,{"derivedFrom":makeQuery(id+"F18.opPattern","COPY",BODY,{"derivedFrom":makeQuery(id+"F11.opExtrude","SWEPT_BODY",BODY,{"disambiguationData":[OSD([sQuery(id+"F10.wireOp",EDGE,"E26"),sQuery(id+"F10.wireOp",EDGE,"E27"),sQuery(id+"F10.wireOp",EDGE,"E28"),sQuery(id+"F10.wireOp",EDGE,"E29")])]}),"instanceName":"1"}),"instanceName":"1"}),"instanceName":"1"}),"instanceName":"1"});
            var Q4;
            Q4=makeQuery(id+"F25.opPattern","COPY",BODY,{"derivedFrom":makeQuery(id+"F24.opPattern","COPY",BODY,{"derivedFrom":makeQuery(id+"F23.opPattern","COPY",BODY,{"derivedFrom":makeQuery(id+"F22.opPattern","COPY",BODY,{"derivedFrom":makeQuery(id+"F16.opExtrude","SWEPT_BODY",BODY,{"disambiguationData":[OSD([sQuery(id+"F15.wireOp",EDGE,"E30.bottom"),sQuery(id+"F15.wireOp",EDGE,"E30.top"),sQuery(id+"F15.wireOp",EDGE,"E30.left"),sQuery(id+"F15.wireOp",EDGE,"E30.right"),sQuery(id+"F15.wireOp",EDGE,"E31.filletArc"),sQuery(id+"F15.wireOp",EDGE,"E32.filletArc"),sQuery(id+"F15.wireOp",EDGE,"E33.filletArc"),sQuery(id+"F15.wireOp",EDGE,"E34.filletArc")])]}),"instanceName":"1"}),"instanceName":"1"}),"instanceName":"1"}),"instanceName":"1"});
            var Q5;
            Q5=makeQuery(id+"F24.opPattern","COPY",BODY,{"derivedFrom":makeQuery(id+"F23.opPattern","COPY",BODY,{"derivedFrom":makeQuery(id+"F22.opPattern","COPY",BODY,{"derivedFrom":makeQuery(id+"F16.opExtrude","SWEPT_BODY",BODY,{"disambiguationData":[OSD([sQuery(id+"F15.wireOp",EDGE,"E30.bottom"),sQuery(id+"F15.wireOp",EDGE,"E30.top"),sQuery(id+"F15.wireOp",EDGE,"E30.left"),sQuery(id+"F15.wireOp",EDGE,"E30.right"),sQuery(id+"F15.wireOp",EDGE,"E31.filletArc"),sQuery(id+"F15.wireOp",EDGE,"E32.filletArc"),sQuery(id+"F15.wireOp",EDGE,"E33.filletArc"),sQuery(id+"F15.wireOp",EDGE,"E34.filletArc")])]}),"instanceName":"1"}),"instanceName":"1"}),"instanceName":"1"});
            var Q6;
            Q6=makeQuery(id+"F20.opPattern","COPY",BODY,{"derivedFrom":makeQuery(id+"F19.opPattern","COPY",BODY,{"derivedFrom":makeQuery(id+"F18.opPattern","COPY",BODY,{"derivedFrom":makeQuery(id+"F11.opExtrude","SWEPT_BODY",BODY,{"disambiguationData":[OSD([sQuery(id+"F10.wireOp",EDGE,"E26"),sQuery(id+"F10.wireOp",EDGE,"E27"),sQuery(id+"F10.wireOp",EDGE,"E28"),sQuery(id+"F10.wireOp",EDGE,"E29")])]}),"instanceName":"1"}),"instanceName":"1"}),"instanceName":"1"});
            var Q7;
            Q7=makeQuery(id+"F23.opPattern","COPY",BODY,{"derivedFrom":makeQuery(id+"F22.opPattern","COPY",BODY,{"derivedFrom":makeQuery(id+"F16.opExtrude","SWEPT_BODY",BODY,{"disambiguationData":[OSD([sQuery(id+"F15.wireOp",EDGE,"E30.bottom"),sQuery(id+"F15.wireOp",EDGE,"E30.top"),sQuery(id+"F15.wireOp",EDGE,"E30.left"),sQuery(id+"F15.wireOp",EDGE,"E30.right"),sQuery(id+"F15.wireOp",EDGE,"E31.filletArc"),sQuery(id+"F15.wireOp",EDGE,"E32.filletArc"),sQuery(id+"F15.wireOp",EDGE,"E33.filletArc"),sQuery(id+"F15.wireOp",EDGE,"E34.filletArc")])]}),"instanceName":"1"}),"instanceName":"1"});
            var Q8;
            Q8=makeQuery(id+"F18.opPattern","COPY",BODY,{"derivedFrom":makeQuery(id+"F11.opExtrude","SWEPT_BODY",BODY,{"disambiguationData":[OSD([sQuery(id+"F10.wireOp",EDGE,"E26"),sQuery(id+"F10.wireOp",EDGE,"E27"),sQuery(id+"F10.wireOp",EDGE,"E28"),sQuery(id+"F10.wireOp",EDGE,"E29")])]}),"instanceName":"1"});
            var Q9;
            Q9=makeQuery(id+"F22.opPattern","COPY",BODY,{"derivedFrom":makeQuery(id+"F16.opExtrude","SWEPT_BODY",BODY,{"disambiguationData":[OSD([sQuery(id+"F15.wireOp",EDGE,"E30.bottom"),sQuery(id+"F15.wireOp",EDGE,"E30.top"),sQuery(id+"F15.wireOp",EDGE,"E30.left"),sQuery(id+"F15.wireOp",EDGE,"E30.right"),sQuery(id+"F15.wireOp",EDGE,"E31.filletArc"),sQuery(id+"F15.wireOp",EDGE,"E32.filletArc"),sQuery(id+"F15.wireOp",EDGE,"E33.filletArc"),sQuery(id+"F15.wireOp",EDGE,"E34.filletArc")])]}),"instanceName":"1"});
            var Q10;
            Q10=makeQuery(id+"F11.opExtrude","SWEPT_BODY",BODY,{"disambiguationData":[OSD([sQuery(id+"F10.wireOp",EDGE,"E26"),sQuery(id+"F10.wireOp",EDGE,"E27"),sQuery(id+"F10.wireOp",EDGE,"E28"),sQuery(id+"F10.wireOp",EDGE,"E29")])]});
            var Q11;
            Q11=makeQuery(id+"F16.opExtrude","SWEPT_BODY",BODY,{"disambiguationData":[OSD([sQuery(id+"F15.wireOp",EDGE,"E30.bottom"),sQuery(id+"F15.wireOp",EDGE,"E30.top"),sQuery(id+"F15.wireOp",EDGE,"E30.left"),sQuery(id+"F15.wireOp",EDGE,"E30.right"),sQuery(id+"F15.wireOp",EDGE,"E31.filletArc"),sQuery(id+"F15.wireOp",EDGE,"E32.filletArc"),sQuery(id+"F15.wireOp",EDGE,"E33.filletArc"),sQuery(id+"F15.wireOp",EDGE,"E34.filletArc")])]});
            var Q12;
            Q12=makeQuery(id+"F27.opExtrude","SWEPT_BODY",BODY,{"disambiguationData":[OSD([sQuery(id+"F26.wireOp",EDGE,"E35.bottom"),sQuery(id+"F26.wireOp",EDGE,"E35.top"),sQuery(id+"F26.wireOp",EDGE,"E35.left"),sQuery(id+"F26.wireOp",EDGE,"E35.right"),sQuery(id+"F26.wireOp",EDGE,"E36.filletArc"),sQuery(id+"F26.wireOp",EDGE,"E37.filletArc"),sQuery(id+"F26.wireOp",EDGE,"E38.filletArc"),sQuery(id+"F26.wireOp",EDGE,"E39.filletArc"),sQuery(id+"F26.wireOp",EDGE,"E40"),sQuery(id+"F26.wireOp",EDGE,"E41")])]});
            var Q13;
            Q13=makeQuery(id+"F29.opExtrude","SWEPT_BODY",BODY,{"disambiguationData":[OSD([sQuery(id+"F28.wireOp",EDGE,"E42.bottom"),sQuery(id+"F28.wireOp",EDGE,"E42.top"),sQuery(id+"F28.wireOp",EDGE,"E42.left"),sQuery(id+"F28.wireOp",EDGE,"E42.right"),sQuery(id+"F28.wireOp",EDGE,"E43"),sQuery(id+"F28.wireOp",EDGE,"E44"),sQuery(id+"F28.wireOp",EDGE,"E45.filletArc"),sQuery(id+"F28.wireOp",EDGE,"E46.filletArc"),sQuery(id+"F28.wireOp",EDGE,"E47.filletArc"),sQuery(id+"F28.wireOp",EDGE,"E48.filletArc")])]});
            transform(context, id + "F32", {"entities" : qUnion([Q0, Q1, Q2, Q3, Q4, Q5, Q6, Q7, Q8, Q9, Q10, Q11, Q12, Q13]), "transformType" : TransformType.TRANSLATION_3D, "dx" : -1860 * mm, "dy" : 0 * mm, "dz" : 0 * mm, "makeCopy" : true});
        }
        {
            var Q0;
            Q0=makeQuery(id+"F31.opPattern","COPY",BODY,{"derivedFrom":makeQuery(id+"F4.opExtrude","SWEPT_BODY",BODY,{"disambiguationData":[OSD([sQuery(id+"F3.wireOp",EDGE,"E9"),sQuery(id+"F3.wireOp",EDGE,"E10"),sQuery(id+"F3.wireOp",EDGE,"E11"),sQuery(id+"F3.wireOp",EDGE,"E12")])]}),"instanceName":"1"});
            var Q1;
            Q1=makeQuery(id+"F31.opPattern","COPY",BODY,{"derivedFrom":makeQuery(id+"F9.opExtrude","SWEPT_BODY",BODY,{"disambiguationData":[OSD([sQuery(id+"F8.wireOp",EDGE,"E14.0.0"),sQuery(id+"F8.wireOp",EDGE,"E14.0.1"),sQuery(id+"F8.wireOp",EDGE,"E14.0.2"),sQuery(id+"F8.wireOp",EDGE,"E14.0.3"),sQuery(id+"F8.wireOp",EDGE,"E14.0.4"),sQuery(id+"F8.wireOp",EDGE,"E14.0.5"),sQuery(id+"F8.wireOp",EDGE,"E14.0.6"),sQuery(id+"F8.wireOp",EDGE,"E14.0.7"),sQuery(id+"F8.wireOp",EDGE,"E15.0"),sQuery(id+"F8.wireOp",EDGE,"E17.0"),sQuery(id+"F8.wireOp",EDGE,"E18.0"),sQuery(id+"F8.wireOp",EDGE,"E20.0"),sQuery(id+"F8.wireOp",EDGE,"E21.0"),sQuery(id+"F8.wireOp",EDGE,"E22.0"),sQuery(id+"F8.wireOp",EDGE,"E23.0"),sQuery(id+"F8.wireOp",EDGE,"E24.0")])]}),"instanceName":"1"});
            var Q2;
            Q2=makeQuery(id+"F31.opPattern","COPY",BODY,{"derivedFrom":makeQuery(id+"F21.opPattern","COPY",BODY,{"derivedFrom":makeQuery(id+"F20.opPattern","COPY",BODY,{"derivedFrom":makeQuery(id+"F19.opPattern","COPY",BODY,{"derivedFrom":makeQuery(id+"F18.opPattern","COPY",BODY,{"derivedFrom":makeQuery(id+"F11.opExtrude","SWEPT_BODY",BODY,{"disambiguationData":[OSD([sQuery(id+"F10.wireOp",EDGE,"E26"),sQuery(id+"F10.wireOp",EDGE,"E27"),sQuery(id+"F10.wireOp",EDGE,"E28"),sQuery(id+"F10.wireOp",EDGE,"E29")])]}),"instanceName":"1"}),"instanceName":"1"}),"instanceName":"1"}),"instanceName":"1"}),"instanceName":"1"});
            var Q3;
            Q3=makeQuery(id+"F31.opPattern","COPY",BODY,{"derivedFrom":makeQuery(id+"F25.opPattern","COPY",BODY,{"derivedFrom":makeQuery(id+"F24.opPattern","COPY",BODY,{"derivedFrom":makeQuery(id+"F23.opPattern","COPY",BODY,{"derivedFrom":makeQuery(id+"F22.opPattern","COPY",BODY,{"derivedFrom":makeQuery(id+"F16.opExtrude","SWEPT_BODY",BODY,{"disambiguationData":[OSD([sQuery(id+"F15.wireOp",EDGE,"E30.bottom"),sQuery(id+"F15.wireOp",EDGE,"E30.top"),sQuery(id+"F15.wireOp",EDGE,"E30.left"),sQuery(id+"F15.wireOp",EDGE,"E30.right"),sQuery(id+"F15.wireOp",EDGE,"E31.filletArc"),sQuery(id+"F15.wireOp",EDGE,"E32.filletArc"),sQuery(id+"F15.wireOp",EDGE,"E33.filletArc"),sQuery(id+"F15.wireOp",EDGE,"E34.filletArc")])]}),"instanceName":"1"}),"instanceName":"1"}),"instanceName":"1"}),"instanceName":"1"}),"instanceName":"1"});
            var Q4;
            Q4=makeQuery(id+"F31.opPattern","COPY",BODY,{"derivedFrom":makeQuery(id+"F20.opPattern","COPY",BODY,{"derivedFrom":makeQuery(id+"F19.opPattern","COPY",BODY,{"derivedFrom":makeQuery(id+"F18.opPattern","COPY",BODY,{"derivedFrom":makeQuery(id+"F11.opExtrude","SWEPT_BODY",BODY,{"disambiguationData":[OSD([sQuery(id+"F10.wireOp",EDGE,"E26"),sQuery(id+"F10.wireOp",EDGE,"E27"),sQuery(id+"F10.wireOp",EDGE,"E28"),sQuery(id+"F10.wireOp",EDGE,"E29")])]}),"instanceName":"1"}),"instanceName":"1"}),"instanceName":"1"}),"instanceName":"1"});
            var Q5;
            Q5=makeQuery(id+"F31.opPattern","COPY",BODY,{"derivedFrom":makeQuery(id+"F24.opPattern","COPY",BODY,{"derivedFrom":makeQuery(id+"F23.opPattern","COPY",BODY,{"derivedFrom":makeQuery(id+"F22.opPattern","COPY",BODY,{"derivedFrom":makeQuery(id+"F16.opExtrude","SWEPT_BODY",BODY,{"disambiguationData":[OSD([sQuery(id+"F15.wireOp",EDGE,"E30.bottom"),sQuery(id+"F15.wireOp",EDGE,"E30.top"),sQuery(id+"F15.wireOp",EDGE,"E30.left"),sQuery(id+"F15.wireOp",EDGE,"E30.right"),sQuery(id+"F15.wireOp",EDGE,"E31.filletArc"),sQuery(id+"F15.wireOp",EDGE,"E32.filletArc"),sQuery(id+"F15.wireOp",EDGE,"E33.filletArc"),sQuery(id+"F15.wireOp",EDGE,"E34.filletArc")])]}),"instanceName":"1"}),"instanceName":"1"}),"instanceName":"1"}),"instanceName":"1"});
            var Q6;
            Q6=makeQuery(id+"F31.opPattern","COPY",BODY,{"derivedFrom":makeQuery(id+"F19.opPattern","COPY",BODY,{"derivedFrom":makeQuery(id+"F18.opPattern","COPY",BODY,{"derivedFrom":makeQuery(id+"F11.opExtrude","SWEPT_BODY",BODY,{"disambiguationData":[OSD([sQuery(id+"F10.wireOp",EDGE,"E26"),sQuery(id+"F10.wireOp",EDGE,"E27"),sQuery(id+"F10.wireOp",EDGE,"E28"),sQuery(id+"F10.wireOp",EDGE,"E29")])]}),"instanceName":"1"}),"instanceName":"1"}),"instanceName":"1"});
            var Q7;
            Q7=makeQuery(id+"F31.opPattern","COPY",BODY,{"derivedFrom":makeQuery(id+"F23.opPattern","COPY",BODY,{"derivedFrom":makeQuery(id+"F22.opPattern","COPY",BODY,{"derivedFrom":makeQuery(id+"F16.opExtrude","SWEPT_BODY",BODY,{"disambiguationData":[OSD([sQuery(id+"F15.wireOp",EDGE,"E30.bottom"),sQuery(id+"F15.wireOp",EDGE,"E30.top"),sQuery(id+"F15.wireOp",EDGE,"E30.left"),sQuery(id+"F15.wireOp",EDGE,"E30.right"),sQuery(id+"F15.wireOp",EDGE,"E31.filletArc"),sQuery(id+"F15.wireOp",EDGE,"E32.filletArc"),sQuery(id+"F15.wireOp",EDGE,"E33.filletArc"),sQuery(id+"F15.wireOp",EDGE,"E34.filletArc")])]}),"instanceName":"1"}),"instanceName":"1"}),"instanceName":"1"});
            var Q8;
            Q8=makeQuery(id+"F31.opPattern","COPY",BODY,{"derivedFrom":makeQuery(id+"F22.opPattern","COPY",BODY,{"derivedFrom":makeQuery(id+"F16.opExtrude","SWEPT_BODY",BODY,{"disambiguationData":[OSD([sQuery(id+"F15.wireOp",EDGE,"E30.bottom"),sQuery(id+"F15.wireOp",EDGE,"E30.top"),sQuery(id+"F15.wireOp",EDGE,"E30.left"),sQuery(id+"F15.wireOp",EDGE,"E30.right"),sQuery(id+"F15.wireOp",EDGE,"E31.filletArc"),sQuery(id+"F15.wireOp",EDGE,"E32.filletArc"),sQuery(id+"F15.wireOp",EDGE,"E33.filletArc"),sQuery(id+"F15.wireOp",EDGE,"E34.filletArc")])]}),"instanceName":"1"}),"instanceName":"1"});
            var Q9;
            Q9=makeQuery(id+"F31.opPattern","COPY",BODY,{"derivedFrom":makeQuery(id+"F18.opPattern","COPY",BODY,{"derivedFrom":makeQuery(id+"F11.opExtrude","SWEPT_BODY",BODY,{"disambiguationData":[OSD([sQuery(id+"F10.wireOp",EDGE,"E26"),sQuery(id+"F10.wireOp",EDGE,"E27"),sQuery(id+"F10.wireOp",EDGE,"E28"),sQuery(id+"F10.wireOp",EDGE,"E29")])]}),"instanceName":"1"}),"instanceName":"1"});
            var Q10;
            Q10=makeQuery(id+"F31.opPattern","COPY",BODY,{"derivedFrom":makeQuery(id+"F11.opExtrude","SWEPT_BODY",BODY,{"disambiguationData":[OSD([sQuery(id+"F10.wireOp",EDGE,"E26"),sQuery(id+"F10.wireOp",EDGE,"E27"),sQuery(id+"F10.wireOp",EDGE,"E28"),sQuery(id+"F10.wireOp",EDGE,"E29")])]}),"instanceName":"1"});
            var Q11;
            Q11=makeQuery(id+"F31.opPattern","COPY",BODY,{"derivedFrom":makeQuery(id+"F16.opExtrude","SWEPT_BODY",BODY,{"disambiguationData":[OSD([sQuery(id+"F15.wireOp",EDGE,"E30.bottom"),sQuery(id+"F15.wireOp",EDGE,"E30.top"),sQuery(id+"F15.wireOp",EDGE,"E30.left"),sQuery(id+"F15.wireOp",EDGE,"E30.right"),sQuery(id+"F15.wireOp",EDGE,"E31.filletArc"),sQuery(id+"F15.wireOp",EDGE,"E32.filletArc"),sQuery(id+"F15.wireOp",EDGE,"E33.filletArc"),sQuery(id+"F15.wireOp",EDGE,"E34.filletArc")])]}),"instanceName":"1"});
            var Q12;
            Q12=makeQuery(id+"F31.opPattern","COPY",BODY,{"derivedFrom":makeQuery(id+"F27.opExtrude","SWEPT_BODY",BODY,{"disambiguationData":[OSD([sQuery(id+"F26.wireOp",EDGE,"E35.bottom"),sQuery(id+"F26.wireOp",EDGE,"E35.top"),sQuery(id+"F26.wireOp",EDGE,"E35.left"),sQuery(id+"F26.wireOp",EDGE,"E35.right"),sQuery(id+"F26.wireOp",EDGE,"E36.filletArc"),sQuery(id+"F26.wireOp",EDGE,"E37.filletArc"),sQuery(id+"F26.wireOp",EDGE,"E38.filletArc"),sQuery(id+"F26.wireOp",EDGE,"E39.filletArc"),sQuery(id+"F26.wireOp",EDGE,"E40"),sQuery(id+"F26.wireOp",EDGE,"E41")])]}),"instanceName":"1"});
            var Q13;
            Q13=makeQuery(id+"F31.opPattern","COPY",BODY,{"derivedFrom":makeQuery(id+"F29.opExtrude","SWEPT_BODY",BODY,{"disambiguationData":[OSD([sQuery(id+"F28.wireOp",EDGE,"E42.bottom"),sQuery(id+"F28.wireOp",EDGE,"E42.top"),sQuery(id+"F28.wireOp",EDGE,"E42.left"),sQuery(id+"F28.wireOp",EDGE,"E42.right"),sQuery(id+"F28.wireOp",EDGE,"E43"),sQuery(id+"F28.wireOp",EDGE,"E44"),sQuery(id+"F28.wireOp",EDGE,"E45.filletArc"),sQuery(id+"F28.wireOp",EDGE,"E46.filletArc"),sQuery(id+"F28.wireOp",EDGE,"E47.filletArc"),sQuery(id+"F28.wireOp",EDGE,"E48.filletArc")])]}),"instanceName":"1"});
            transform(context, id + "F33", {"entities" : qUnion([Q0, Q1, Q2, Q3, Q4, Q5, Q6, Q7, Q8, Q9, Q10, Q11, Q12, Q13]), "transformType" : TransformType.TRANSLATION_3D, "dx" : -900 * mm, "dy" : 0 * mm, "dz" : 0 * mm, "makeCopy" : true});
        }
    });
